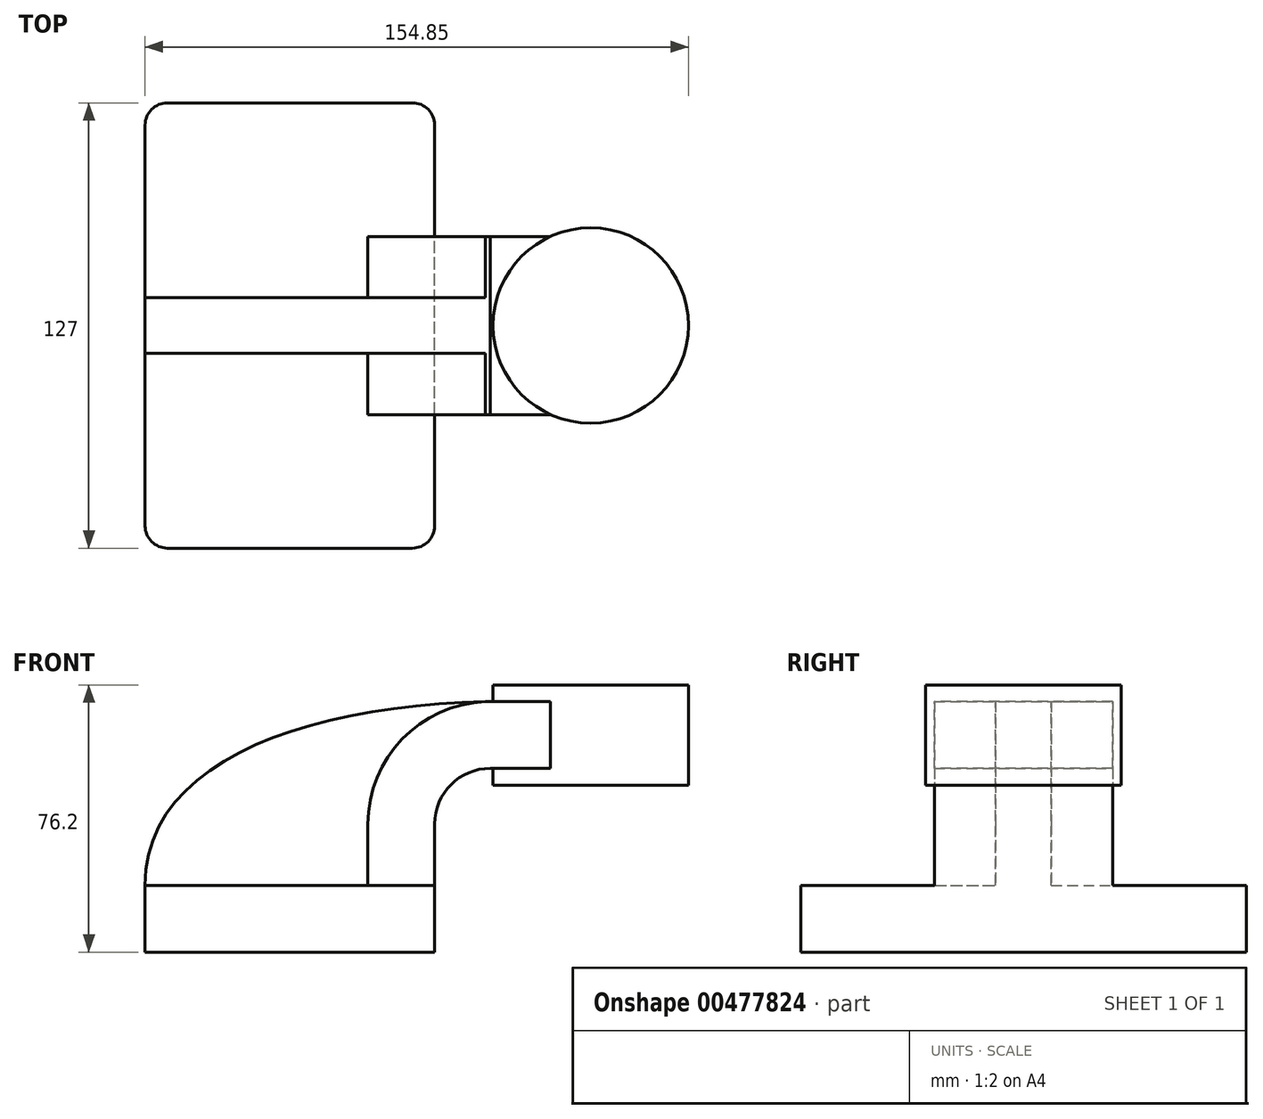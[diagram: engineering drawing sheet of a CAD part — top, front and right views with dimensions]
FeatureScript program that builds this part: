
annotation { "Feature Type Name" : "Feature", "Feature Type Description" : "" }
export const myFeature = defineFeature(function(context is Context, id is Id, definition is map)
    precondition{}
    {
        {
            var Q0;
            Q0=qCreatedBy(makeId("Front.planeOp"),FACE);
            var sketch = newSketch(context, id + "F0", { "sketchPlane" : qUnion([Q0])});
            skLineSegment(sketch, "E0.bottom", {"start": v(-38.6, 11.98) * mm, "end": v(43.95, 11.98) * mm});
            skLineSegment(sketch, "E0.top", {"start": v(-38.6, -7.07) * mm, "end": v(43.95, -7.07) * mm});
            skLineSegment(sketch, "E0.left", {"start": v(-38.6, 11.98) * mm, "end": v(-38.6, -7.07) * mm});
            skLineSegment(sketch, "E0.right", {"start": v(43.95, 11.98) * mm, "end": v(43.95, -7.07) * mm});
            skLineSegment(sketch, "E1", {"start": v(43.95, 11.98) * mm, "end": v(43.95, 29.46) * mm});
            skArc(sketch, "E2", {"start": v(43.95, 29.46) * mm, "mid": v(48.6, 40.68) * mm, "end": v(59.83, 45.33) * mm});
            skLineSegment(sketch, "E3", {"start": v(59.83, 45.33) * mm, "end": v(88.4, 45.33) * mm});
            skLineSegment(sketch, "E4.bottom", {"start": v(65.45, 69.13) * mm, "end": v(116.25, 69.13) * mm});
            skLineSegment(sketch, "E4.top", {"start": v(65.45, 40.56) * mm, "end": v(116.25, 40.56) * mm});
            skLineSegment(sketch, "E4.right", {"start": v(116.25, 69.13) * mm, "end": v(116.25, 40.56) * mm});
            skArc(sketch, "E5.0", {"start": v(24.9, 29.46) * mm, "mid": v(35.13, 54.15) * mm, "end": v(59.83, 64.38) * mm});
            skLineSegment(sketch, "E6", {"start": v(24.9, 29.46) * mm, "end": v(24.9, 11.98) * mm});
            skLineSegment(sketch, "E7", {"start": v(59.83, 64.38) * mm, "end": v(88.4, 64.38) * mm});
            skFitSpline(sketch, "E8", {"points": [v(-38.6, 11.98) * mm, v(59.83, 64.38) * mm], "startDerivative": vector(-0.6, 106.62) * mm, "endDerivative": vector(156.01, 2.75) * mm});
            skLineSegment(sketch, "E9", {"start": v(65.45, 69.13) * mm, "end": v(65.45, 64.38) * mm});
            skLineSegment(sketch, "E10", {"start": v(65.52, 45.33) * mm, "end": v(65.45, 40.56) * mm});
            skLineSegment(sketch, "E11", {"start": v(88.4, 69.13) * mm, "end": v(88.4, 40.56) * mm});
            skSolve(sketch);
        }
        {
            var Q0;
            Q0=makeQuery(id+"F0.imprint","IMPRINT",FACE,{"disambiguationData":[TD([[makeQuery(id+"F0.imprint","IMPRINT",EDGE,{"derivedFrom":sQuery(id+"F0.wireOp",EDGE,"E0.top")}),1.0]])]});
            extrude(context, id + "F1", {"entities" : qUnion([Q0]), "endBound" : BoundingType.SYMMETRIC, "depth" : 127 * mm});
        }
        {
            var Q0;
            {var subQ9=sQuery(id+"F0.wireOp",EDGE,"E1");Q0=makeQuery(id+"F0.imprint","IMPRINT",FACE,{"disambiguationData":[TD([[makeQuery(id+"F0.imprint","IMPRINT",EDGE,{"derivedFrom":subQ9}),1.0]])]});}
            var Q1;
            {var subQ0=sQuery(id+"F0.wireOp",EDGE,"401mmgxn-GKza-u9Tz-tDkY-5sWQWdLDGwaR");Q1=makeQuery(id+"F0.imprint","IMPRINT",FACE,{"disambiguationData":[TD([[makeQuery(id+"F0.imprint","IMPRINT",EDGE,{"derivedFrom":subQ0}),1.0]])]});}
            extrude(context, id + "F2", {"entities" : qUnion([Q0, Q1]), "operationType" : NewBodyOperationType.ADD, "endBound" : BoundingType.SYMMETRIC, "depth" : 50.8 * mm});
        }
        {
            var Q0;
            {var subQ3=sQuery(id+"F0.wireOp",EDGE,"E6");Q0=makeQuery(id+"F0.imprint","IMPRINT",FACE,{"disambiguationData":[TD([[makeQuery(id+"F0.imprint","IMPRINT",EDGE,{"derivedFrom":subQ3}),-1.0]])]});}
            extrude(context, id + "F3", {"entities" : qUnion([Q0]), "operationType" : NewBodyOperationType.ADD, "endBound" : BoundingType.SYMMETRIC, "depth" : 15.88 * mm});
        }
        {
            var Q0;
            {var subQ4=sQuery(id+"F0.wireOp",EDGE,"E4.right");Q0=makeQuery(id+"F0.imprint","IMPRINT",FACE,{"disambiguationData":[TD([[makeQuery(id+"F0.imprint","IMPRINT",EDGE,{"derivedFrom":subQ4}),-1.0]])]});}
            var Q1;
            Q1=sQuery(id+"F0.wireOp",EDGE,"E11");
            revolve(context, id + "F4", {"operationType" : NewBodyOperationType.ADD, "entities" : qUnion([Q0]), "axis" : qUnion([Q1]), "revolveType" : RevolveType.FULL});
        }
        {
            var Q0;
            Q0=makeQuery(id+"F1.opExtrude","CAP_EDGE",EDGE,{"disambiguationData":[OSD([sQuery(id+"F0.wireOp",EDGE,"E0.left")])],"isStart":false});
            var Q1;
            Q1=makeQuery(id+"F1.opExtrude","CAP_EDGE",EDGE,{"disambiguationData":[OSD([sQuery(id+"F0.wireOp",EDGE,"E0.right")])],"isStart":false});
            var Q2;
            Q2=makeQuery(id+"F1.opExtrude","CAP_EDGE",EDGE,{"disambiguationData":[OSD([sQuery(id+"F0.wireOp",EDGE,"E0.left")])],"isStart":true});
            var Q3;
            Q3=makeQuery(id+"F1.opExtrude","CAP_EDGE",EDGE,{"disambiguationData":[OSD([sQuery(id+"F0.wireOp",EDGE,"E0.right")])],"isStart":true});
            fillet(context, id + "F5", {"entities" : qUnion([Q0, Q1, Q2, Q3]), "radius" : 6.35 * mm, "tangentPropagation" : true, "allowEdgeOverflow" : false});
        }
    });
